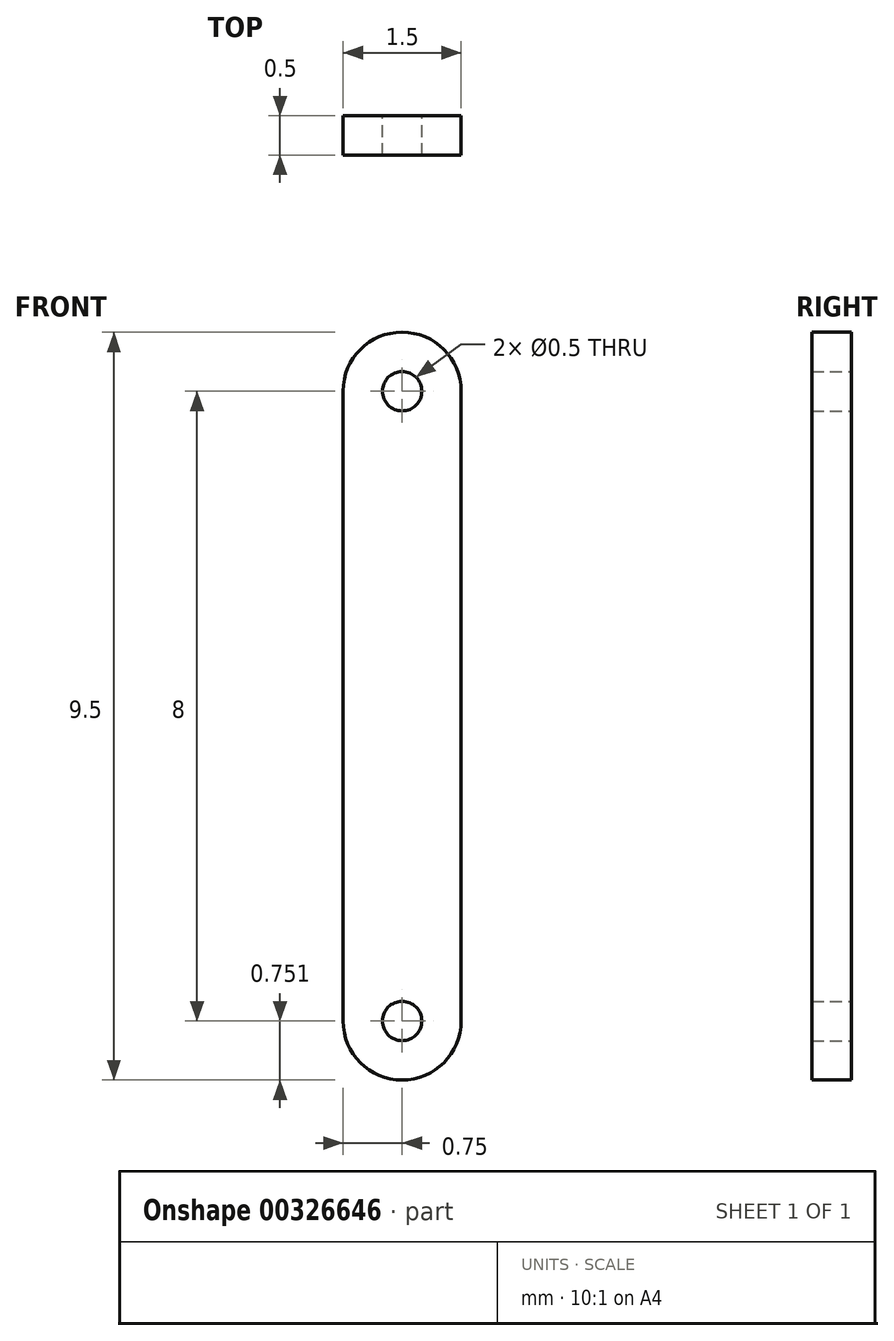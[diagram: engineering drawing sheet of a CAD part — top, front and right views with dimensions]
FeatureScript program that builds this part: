
annotation { "Feature Type Name" : "Feature", "Feature Type Description" : "" }
export const myFeature = defineFeature(function(context is Context, id is Id, definition is map)
    precondition{}
    {
        {
            var Q0;
            Q0=qCreatedBy(makeId("Front.planeOp"),FACE);
            var sketch = newSketch(context, id + "F0", { "sketchPlane" : qUnion([Q0])});
            skCircle(sketch, "E0", {"center": v(0, 39.92) * mm, "radius": 0.25 * mm});
            skLineSegment(sketch, "E1", {"start": v(-0.75, 39.92) * mm, "end": v(-0.75, 31.92) * mm});
            skLineSegment(sketch, "E2.MirrorCS", {"start": v(0.75, 39.92) * mm, "end": v(0.75, 31.92) * mm});
            skArc(sketch, "E3", {"start": v(0.75, 39.92) * mm, "mid": v(0, 40.67) * mm, "end": v(-0.75, 39.92) * mm});
            skArc(sketch, "E4.MirrorCS", {"start": v(-0.75, 39.92) * mm, "mid": v(0, 40.67) * mm, "end": v(0.75, 39.92) * mm});
            skCircle(sketch, "E5", {"center": v(0, 31.92) * mm, "radius": 0.25 * mm, "construction": true});
            skArc(sketch, "E6", {"start": v(-0.75, 31.92) * mm, "mid": v(0, 31.17) * mm, "end": v(0.75, 31.92) * mm, "construction": true});
            skArc(sketch, "E7", {"start": v(0.75, 31.92) * mm, "mid": v(0, 31.17) * mm, "end": v(-0.75, 31.92) * mm});
            skCircle(sketch, "E8", {"center": v(0, 31.92) * mm, "radius": 0.25 * mm});
            skSolve(sketch);
        }
        {
            var Q0;
            Q0=makeQuery(id+"F0.imprint","IMPRINT",FACE,{"disambiguationData":[TD([[makeQuery(id+"F0.imprint","IMPRINT",EDGE,{"derivedFrom":sQuery(id+"F0.wireOp",EDGE,"E1")}),1.0]])]});
            extrude(context, id + "F1", {"entities" : qUnion([Q0]), "depth" : .5 * mm});
        }
    });
